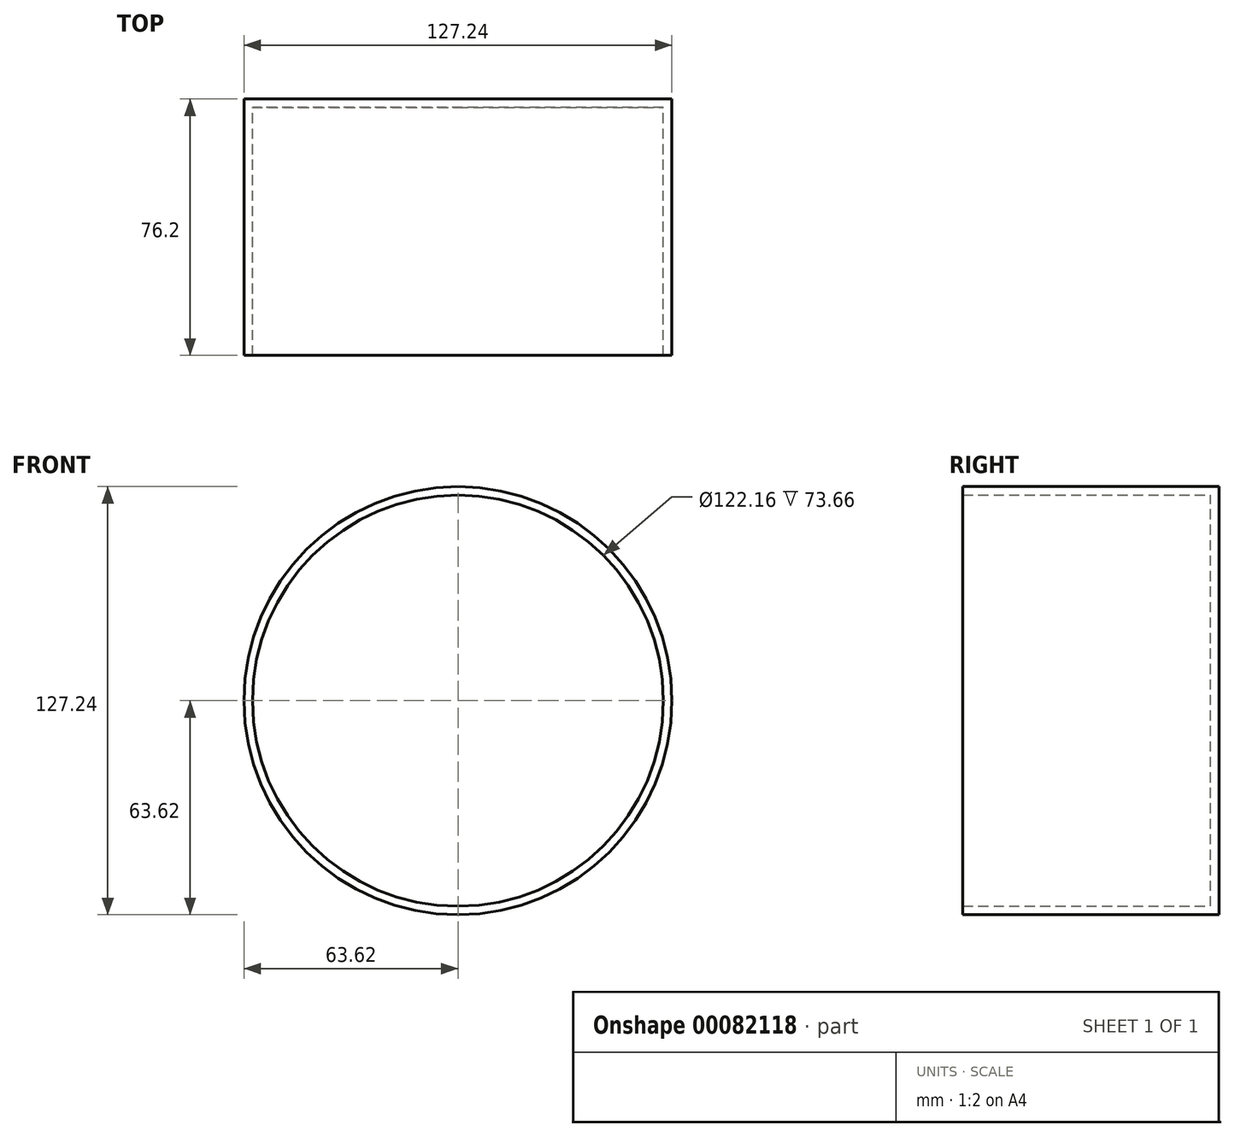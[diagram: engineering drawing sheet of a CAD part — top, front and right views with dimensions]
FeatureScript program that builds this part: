
annotation { "Feature Type Name" : "Feature", "Feature Type Description" : "" }
export const myFeature = defineFeature(function(context is Context, id is Id, definition is map)
    precondition{}
    {
        {
            var Q0;
            Q0=qCreatedBy(makeId("Front.planeOp"),FACE);
            var sketch = newSketch(context, id + "F0", { "sketchPlane" : qUnion([Q0])});
            skCircle(sketch, "E0", {"center": v(0, 0) * mm, "radius": 63.62 * mm});
            skSolve(sketch);
        }
        {
            var Q0;
            Q0=makeQuery(id+"F0.imprint","IMPRINT",FACE,{"disambiguationData":[TD([[makeQuery(id+"F0.imprint","IMPRINT",EDGE,{"derivedFrom":sQuery(id+"F0.wireOp",EDGE,"E0")}),1.0]])]});
            extrude(context, id + "F1", {"entities" : qUnion([Q0]), "endBound" : BoundingType.SYMMETRIC, "depth" : 76.2 * mm});
        }
        {
            var Q0;
            Q0=qCreatedBy(makeId("Front.planeOp"),FACE);
            var sketch = newSketch(context, id + "F2", { "sketchPlane" : qUnion([Q0])});
            skCircle(sketch, "E1", {"center": v(-29.27, 20.6) * mm, "radius": 11.23 * mm});
            skCircle(sketch, "E2", {"center": v(17, 19.75) * mm, "radius": 14.4 * mm});
            skLineSegment(sketch, "E3", {"start": v(-31, -14.04) * mm, "end": v(-17.86, -24.59) * mm});
            skLineSegment(sketch, "E4", {"start": v(-17.86, -24.59) * mm, "end": v(0, -27.39) * mm});
            skLineSegment(sketch, "E5", {"start": v(0, -27.39) * mm, "end": v(15.07, -24.59) * mm});
            skLineSegment(sketch, "E6", {"start": v(15.07, -24.59) * mm, "end": v(26.47, -12.97) * mm});
            skLineSegment(sketch, "E7", {"start": v(-31, -16.2) * mm, "end": v(-19.58, -37.29) * mm});
            skLineSegment(sketch, "E8", {"start": v(-19.58, -37.29) * mm, "end": v(9.9, -39.44) * mm});
            skLineSegment(sketch, "E9", {"start": v(11.4, -39.44) * mm, "end": v(24.32, -30.83) * mm});
            skLineSegment(sketch, "E10", {"start": v(26.47, -12.97) * mm, "end": v(24.32, -30.83) * mm});
            skSolve(sketch);
        }
        {
            var Q0;
            Q0 = qSketchRegion(id + "F2", true);
            extrude(context, id + "F3", {"entities" : qUnion([Q0]), "operationType" : NewBodyOperationType.ADD, "depth" : 25.4 * mm});
        }
        {
            var Q0;
            Q0 = qSketchRegion(id + "F2", true);
            extrude(context, id + "F4", {"entities" : qUnion([Q0]), "operationType" : NewBodyOperationType.ADD, "depth" : 25.4 * mm});
        }
        {
            var Q0;
            Q0=makeQuery(id+"F1.opExtrude","CAP_FACE",FACE,{"disambiguationData":[OSD([sQuery(id+"F0.wireOp",EDGE,"E0")])],"isStart":false});
            shell(context, id + "F5", {"entities" : qUnion([Q0]), "thickness" : 2.54 * mm});
        }
    });
